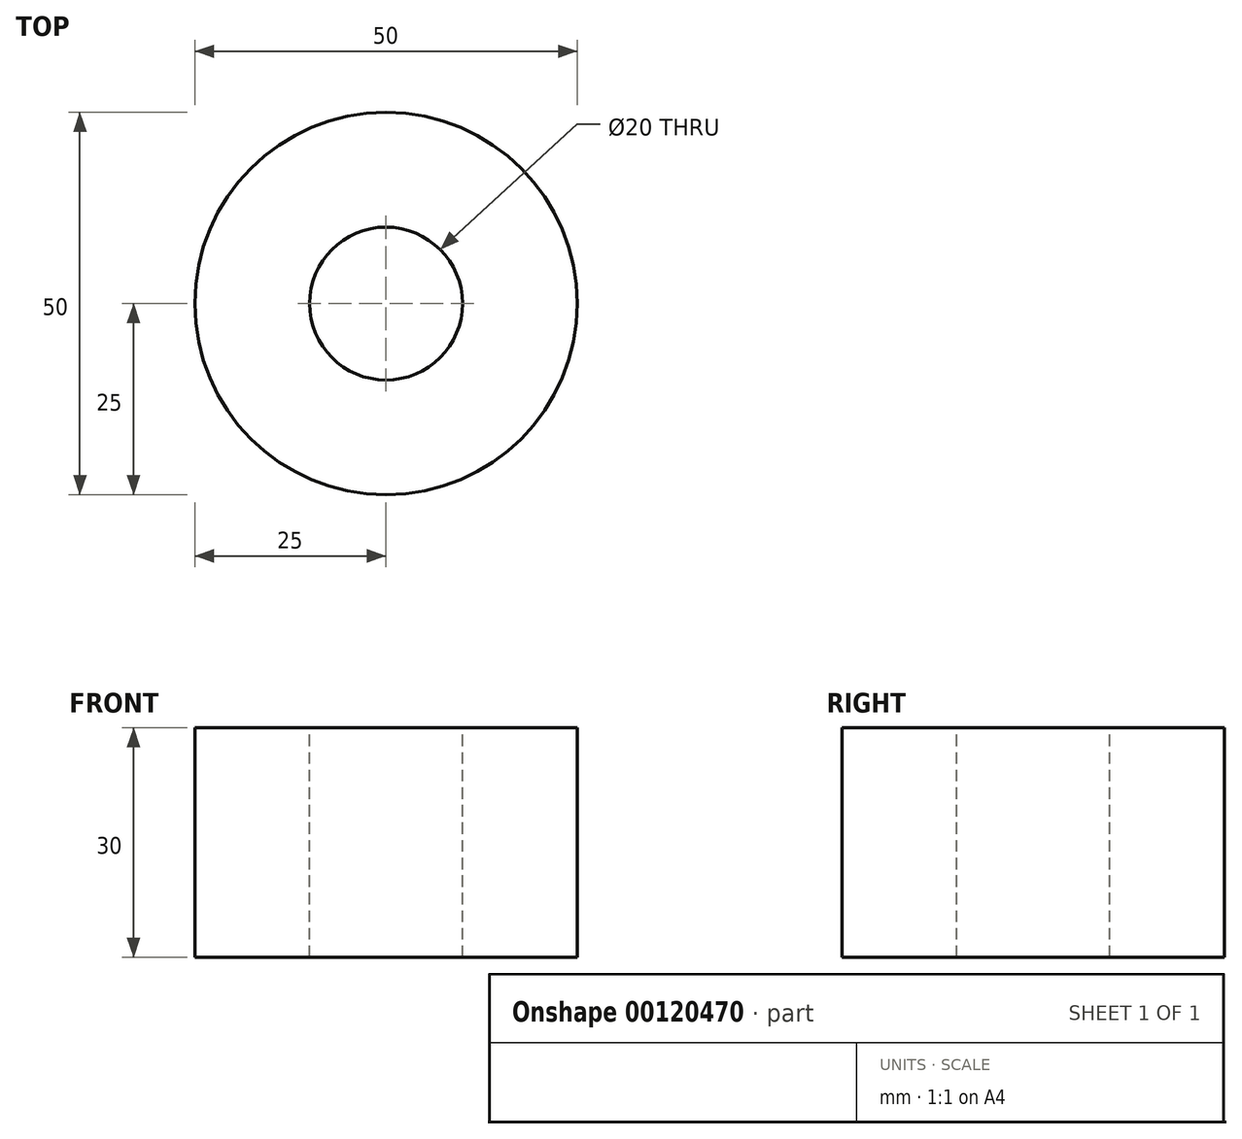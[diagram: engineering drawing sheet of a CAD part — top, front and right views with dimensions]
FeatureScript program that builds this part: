
annotation { "Feature Type Name" : "Feature", "Feature Type Description" : "" }
export const myFeature = defineFeature(function(context is Context, id is Id, definition is map)
    precondition{}
    {
        {
            var Q0;
            Q0=qCreatedBy(makeId("Top.planeOp"),FACE);
            var sketch = newSketch(context, id + "F0", { "sketchPlane" : qUnion([Q0])});
            skCircle(sketch, "E0", {"center": v(0, 0) * mm, "radius": 25 * mm});
            skCircle(sketch, "E1", {"center": v(0, 0) * mm, "radius": 10 * mm});
            skSolve(sketch);
        }
        {
            var Q0;
            Q0=makeQuery(id+"F0.imprint","IMPRINT",FACE,{"disambiguationData":[TD([[makeQuery(id+"F0.imprint","IMPRINT",EDGE,{"derivedFrom":sQuery(id+"F0.wireOp",EDGE,"E0")}),1.0]])]});
            extrude(context, id + "F1", {"entities" : qUnion([Q0]), "oppositeDirection" : true, "depth" : 30 * mm});
        }
    });
